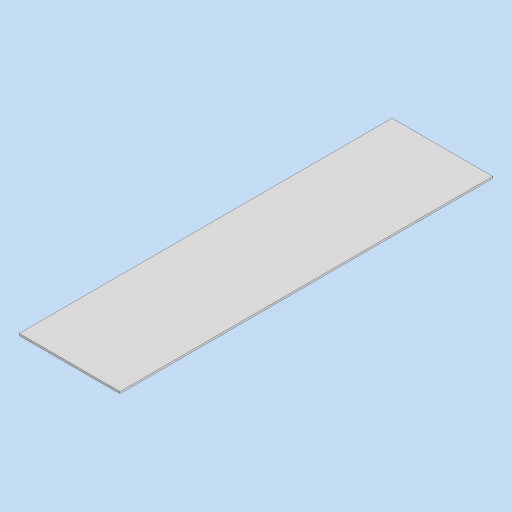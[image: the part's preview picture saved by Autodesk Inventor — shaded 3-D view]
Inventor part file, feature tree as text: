
AUTODESK INVENTOR PART (.ipt)
format: ipt  version: 2023 (Build 270158000, 158)  size: 92,672 bytes
history: native  units: in
note: dims shown in document units (in); Inventor stores cm internally (conversion verified against a paired STEP export)
features: other x1, extrude x1, sketch x1
ambient origin geometry x8: Origin, YZ Plane, XZ Plane, XY Plane, X Axis, Y Axis, Z Axis, Center Point
bodies: Solid1 (feature_tree)
feature tree (3):
  parser-record x1  (decoder bookkeeping rows leaked as tree rows — omitted from the tree; the rows remain in map.json)
  extrude  "Extrusion1"  Depth=23.622in
  sketch  "Sketch1"  dims[d0=6.378in d1=23.622in d2=0.125in d3=0.0in d4=0.0197in d5=0.0344in d6=0.0197in d7=0.0344in]
note: 1 file-system path scrubbed to <path> (originals preserved in map.json)
